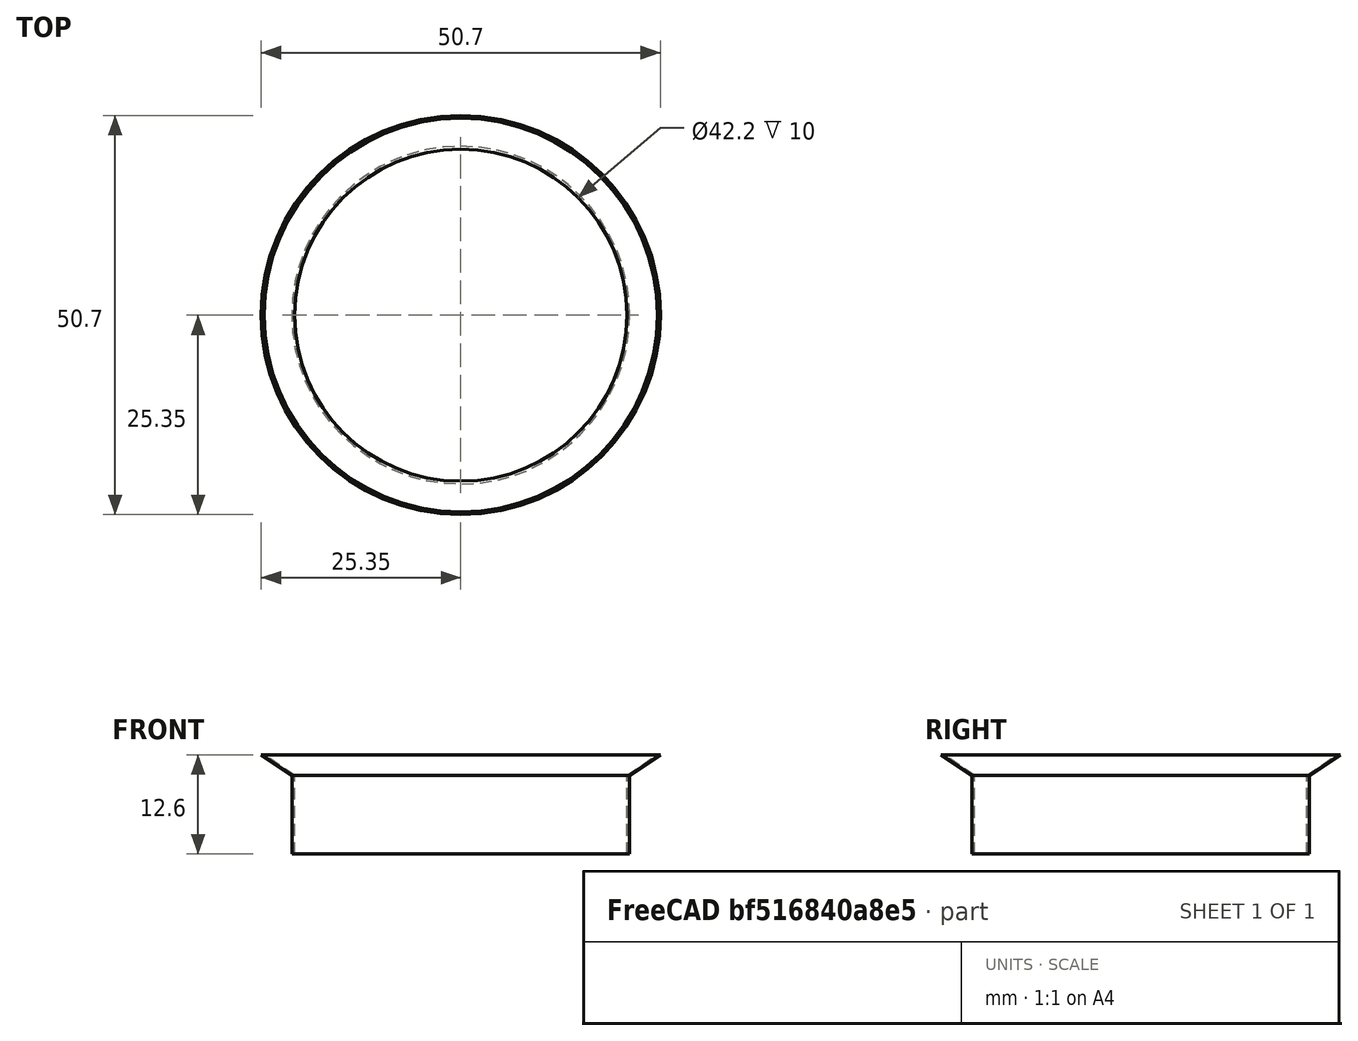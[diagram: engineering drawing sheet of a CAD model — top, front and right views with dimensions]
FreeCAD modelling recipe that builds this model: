
FCSTD DOCUMENT  (FreeCAD 0.17R13519 (Git))
Label: CTASU_LaserWelder_Ring_v1
License: All rights reserved
LicenseURL: http://en.wikipedia.org/wiki/All_rights_reserved
objects: TechDraw::DrawViewDimension×3, Part::Cylinder×2, Part::Cut×2, Part::Cone×2, TechDraw::DrawProjGroupItem×2, TechDraw::DrawSVGTemplate×1, TechDraw::DrawProjGroup×1, TechDraw::DrawPage×1
note: 6 computed .brp shape members not serialized (recipe doc carries the construction recipe); baked Part::Feature solids carry a one-line shape summary decoded from their .brp

FEATURE [Part::Cylinder] Cylinder
  Angle = 360
  AttacherType = Attacher::AttachEngine3D
  Height = 10
  Radius = 21.45
FEATURE [Part::Cylinder] Cylinder001
  Angle = 360
  AttacherType = Attacher::AttachEngine3D
  Height = 10
  Radius = 21.1
FEATURE [Part::Cut] Cut
  Base = -> Cylinder
  Tool = -> Cylinder001
FEATURE [Part::Cone] Cone
  Angle = 360
  AttacherType = Attacher::AttachEngine3D
  Height = 2.6
  Placement = pos=(0,0,10) rot=(0,0,1;0rad)
  Radius1 = 21.45
  Radius2 = 25.35
FEATURE [Part::Cone] Cone001
  Angle = 360
  AttacherType = Attacher::AttachEngine3D
  Height = 2.6
  Placement = pos=(0,0,10) rot=(0,0,1;0rad)
  Radius1 = 21.1
  Radius2 = 25
FEATURE [Part::Cut] Cut001
  Base = -> Cone
  Tool = -> Cone001
FEATURE [TechDraw::DrawSVGTemplate] Template
  EditableTexts = AUTHOR_NAME=AUTHOR NAME; DN=DN; DRAWING_TITLE=DRAWING TITLE; FC-DATE=DD/MM/YYYY; FC-REV=REV A; FC-SC=SCALE; FC-SH=X / Y; FC-SI=A4; FreeCAD_DRAWING=FreeCAD DRAWING; PN=PN
  Height = 297
  Orientation = 0
  Width = 210
FEATURE [TechDraw::DrawProjGroupItem] ProjItem  label="Front"
  CoarseView = true
  Direction = (1,0,0)
  Focus = 100
  HardHidden = true
  IsoCount = 0
  IsoHidden = true
  IsoVisible = true
  LockPosition = false
  Perspective = false
  Rotation = 0
  RotationVector = (0,-1,0)
  ScaleType = 0
  SeamHidden = true
  SeamVisible = false
  SmoothHidden = true
  SmoothVisible = false
  Source = -> [Cut,Cut001]
  Type = 0
  X = 0
  Y = 0
FEATURE [TechDraw::DrawProjGroupItem] ProjItem001  label="Bottom"
  CoarseView = false
  Direction = (0,0,-1)
  Focus = 100
  HardHidden = false
  IsoCount = 0
  IsoHidden = false
  IsoVisible = false
  LockPosition = false
  Perspective = false
  Rotation = 0
  RotationVector = (0,-1,0)
  ScaleType = 0
  SeamHidden = false
  SeamVisible = false
  SmoothHidden = false
  SmoothVisible = false
  Source = -> [Cut,Cut001]
  Type = 5
  X = 0
  Y = 65.7
FEATURE [TechDraw::DrawProjGroup] ProjGroup
  Anchor = -> ProjItem
  AutoDistribute = true
  CubeDirs = (6) [(0,0,-1),(1,1.83697e-16,0),(1.83697e-16,-1,0),(-1,-1.83697e-16,0),(-1.83697e-16,1,0),(0,0,1)]
  CubeRotations = (6) [(-1.83697e-16,-1,0),(-1.83697e-16,-1,0),(1,-1.83697e-16,0),(1.83697e-16,1,0),(-1,1.83697e-16,0),(-1.83697e-16,-1,0)]
  LockPosition = false
  ProjectionType = 0
  Rotation = 0
  ScaleType = 0
  Source = -> [Cut,Cut001]
  Views = -> [ProjItem,ProjItem001]
  X = 105
  Y = 148.5
  spacingX = 15
  spacingY = 15
FEATURE [TechDraw::DrawViewDimension] Dimension
  FormatSpec = %.2f
  LockPosition = false
  MeasureType = 1
  References2D = -> [ProjItem001]
  Rotation = 0
  ScaleType = 0
  Type = 5
  X = -0.535103
  Y = 39.5976
FEATURE [TechDraw::DrawViewDimension] Dimension001
  FormatSpec = %.2f
  LockPosition = false
  MeasureType = 1
  References2D = -> [ProjItem001]
  Rotation = 0
  ScaleType = 0
  Type = 5
  X = -0.71347
  Y = 51.0131
FEATURE [TechDraw::DrawViewDimension] Dimension002
  FormatSpec = %.2f
  LockPosition = false
  MeasureType = 1
  References2D = -> [ProjItem]
  Rotation = 0
  ScaleType = 0
  Type = 2
  X = 37.6356
  Y = -1.96204
FEATURE [TechDraw::DrawPage] Page
  KeepUpdated = true
  ProjectionType = 0
  Template = -> Template
  Views = -> [ProjGroup,Dimension,Dimension001,Dimension002]
